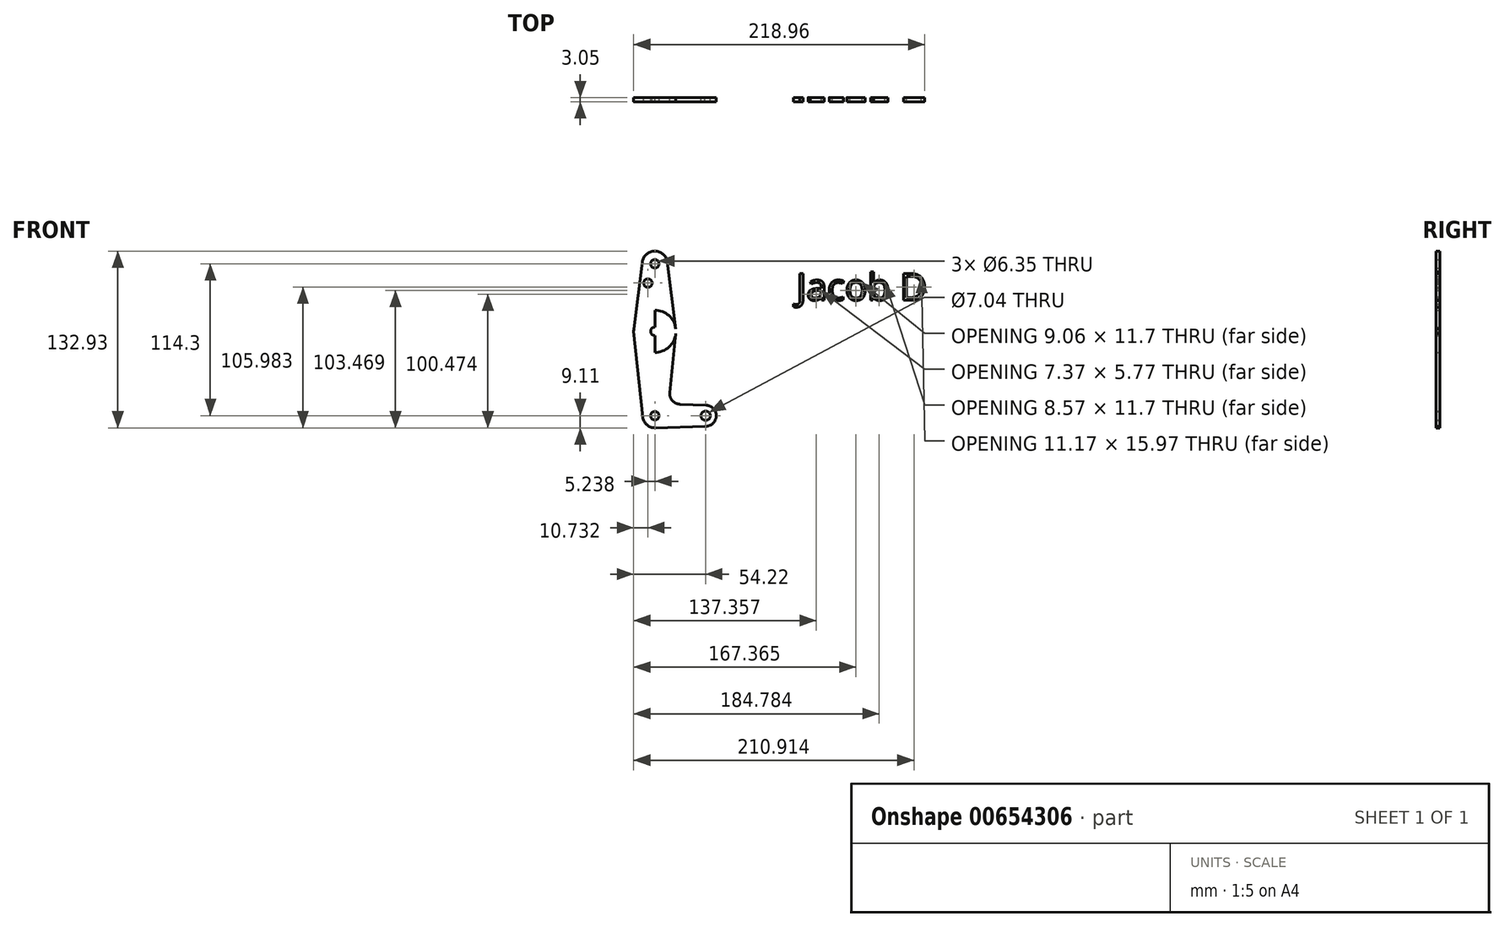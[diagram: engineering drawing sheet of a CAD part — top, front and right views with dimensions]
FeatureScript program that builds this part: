
annotation { "Feature Type Name" : "Feature", "Feature Type Description" : "" }
export const myFeature = defineFeature(function(context is Context, id is Id, definition is map)
    precondition{}
    {
        {
            var Q0;
            Q0=qCreatedBy(makeId("Front.planeOp"),FACE);
            var sketch = newSketch(context, id + "F0", { "sketchPlane" : qUnion([Q0])});
            skLineSegment(sketch, "E0", {"start": v(0, 50.8) * mm, "end": v(0, -63.5) * mm});
            skLineSegment(sketch, "E1", {"start": v(0, -63.5) * mm, "end": v(38.25, -63.5) * mm});
            skCircle(sketch, "E2", {"center": v(0, 50.8) * mm, "radius": 9.53 * mm});
            skCircle(sketch, "E3", {"center": v(0, 0) * mm, "radius": 15.88 * mm});
            skCircle(sketch, "E4", {"center": v(0, -63.5) * mm, "radius": 9.11 * mm});
            skCircle(sketch, "E5", {"center": v(38.25, -63.5) * mm, "radius": 7.94 * mm});
            skLineSegment(sketch, "E6", {"start": v(-15.78, 1.7) * mm, "end": v(-15.97, 0) * mm});
            skLineSegment(sketch, "E7", {"start": v(-15.97, 0) * mm, "end": v(-9.06, -64.47) * mm});
            skLineSegment(sketch, "E8", {"start": v(18.8, -54.84) * mm, "end": v(38.54, -55.57) * mm});
            skLineSegment(sketch, "E9", {"start": v(0.3, -72.6) * mm, "end": v(39.45, -71.35) * mm});
            skLineSegment(sketch, "E10", {"start": v(15.8, -1.63) * mm, "end": v(11.2, -46.08) * mm});
            skCircle(sketch, "E11", {"center": v(0, 50.8) * mm, "radius": 3.18 * mm});
            skCircle(sketch, "E12", {"center": v(-5.24, 36.31) * mm, "radius": 3.18 * mm});
            skCircle(sketch, "E13", {"center": v(38.25, -63.5) * mm, "radius": 3.52 * mm});
            skArc(sketch, "E14.filletArc", {"start": v(11.2, -46.08) * mm, "mid": v(13.1, -52.1) * mm, "end": v(18.8, -54.84) * mm});
            skCircle(sketch, "E15", {"center": v(0, -63.5) * mm, "radius": 3.18 * mm});
            skLineSegment(sketch, "E16", {"start": v(9.45, 52) * mm, "end": v(15.75, 1.98) * mm});
            skLineSegment(sketch, "E17", {"start": v(-9.45, 52) * mm, "end": v(-15.75, 1.98) * mm});
            skCircle(sketch, "E18", {"center": v(0, 0) * mm, "radius": 3.18 * mm});
            skText(sketch, "E19", { "text": "Jacob D", "fontName": "OpenSans-Regular.ttf"});
            const initialGuessF0  = {"E19": [0.10656, 0.02338, 1, 0, 0.02016]};
            skSetInitialGuess(sketch, initialGuessF0);
            skSolve(sketch);
        }
        {
            var Q0;
            {var subQ0=sQuery(id+"F0.wireOp",EDGE,"E7");Q0=makeQuery(id+"F0.imprint","IMPRINT",FACE,{"disambiguationData":[TD([[makeQuery(id+"F0.imprint","IMPRINT",EDGE,{"derivedFrom":subQ0}),1.0]])]});}
            var Q1;
            {var subQ0=sQuery(id+"F0.wireOp",EDGE,"E2");var subQ1=sQuery(id+"F0.wireOp",EDGE,"E0");var subQ2=makeQuery(id+"F0.imprint","INTERSECT",VERTEX,{"derivedFrom":[subQ1,subQ0]});Q1=makeQuery(id+"F0.imprint","IMPRINT",FACE,{"disambiguationData":[TD([[makeQuery(id+"F0.imprint","IMPRINT",EDGE,{"disambiguationData":[TD([[subQ2,-1.0]])],"derivedFrom":subQ1}),1.0]])]});}
            var Q2;
            Q2=makeQuery(id+"F0.imprint","IMPRINT",FACE,{"disambiguationData":[TD([[makeQuery(id+"F0.imprint","IMPRINT",EDGE,{"derivedFrom":sQuery(id+"F0.wireOp",EDGE,"E12")}),-1.0]])]});
            var Q3;
            Q3=makeQuery(id+"F0.imprint","IMPRINT",FACE,{"disambiguationData":[TD([[makeQuery(id+"F0.imprint","IMPRINT",EDGE,{"derivedFrom":sQuery(id+"F0.wireOp",EDGE,"E11")}),-1.0]])]});
            var Q4;
            {var subQ2=sQuery(id+"F0.wireOp",EDGE,"E3");var subQ6=sQuery(id+"F0.wireOp",EDGE,"E0");var subQ8=makeQuery(id+"F0.imprint","INTERSECT",VERTEX,{"disambiguationData":[OD(0.0)],"derivedFrom":[subQ6,subQ2]});Q4=makeQuery(id+"F0.imprint","IMPRINT",FACE,{"disambiguationData":[TD([[makeQuery(id+"F0.imprint","IMPRINT",EDGE,{"disambiguationData":[TD([[subQ8,-1.0]])],"derivedFrom":subQ6}),1.0]])]});}
            var Q5;
            {var subQ0=sQuery(id+"F0.wireOp",EDGE,"E3");var subQ1=sQuery(id+"F0.wireOp",EDGE,"E0");var subQ2=makeQuery(id+"F0.imprint","INTERSECT",VERTEX,{"disambiguationData":[OD(0.0)],"derivedFrom":[subQ1,subQ0]});Q5=makeQuery(id+"F0.imprint","IMPRINT",FACE,{"disambiguationData":[TD([[makeQuery(id+"F0.imprint","IMPRINT",EDGE,{"disambiguationData":[TD([[subQ2,-1.0]])],"derivedFrom":subQ1}),-1.0]])]});}
            var Q6;
            {var subQ0=sQuery(id+"F0.wireOp",EDGE,"E4");var subQ7=sQuery(id+"F0.wireOp",EDGE,"E0");var subQ8=makeQuery(id+"F0.imprint","INTERSECT",VERTEX,{"derivedFrom":[subQ7,subQ0]});Q6=makeQuery(id+"F0.imprint","IMPRINT",FACE,{"disambiguationData":[TD([[makeQuery(id+"F0.imprint","IMPRINT",EDGE,{"disambiguationData":[TD([[subQ8,-1.0]])],"derivedFrom":subQ7}),-1.0]])]});}
            var Q7;
            Q7=makeQuery(id+"F0.imprint","IMPRINT",FACE,{"disambiguationData":[TD([[makeQuery(id+"F0.imprint","IMPRINT",EDGE,{"derivedFrom":sQuery(id+"F0.wireOp",EDGE,"E13")}),-1.0]])]});
            var Q8;
            {var subQ0=sQuery(id+"F0.wireOp",EDGE,"E5");var subQ1=sQuery(id+"F0.wireOp",EDGE,"E1");var subQ2=makeQuery(id+"F0.imprint","INTERSECT",VERTEX,{"derivedFrom":[subQ1,subQ0]});Q8=makeQuery(id+"F0.imprint","IMPRINT",FACE,{"disambiguationData":[TD([[makeQuery(id+"F0.imprint","IMPRINT",EDGE,{"disambiguationData":[TD([[subQ2,1.0]])],"derivedFrom":subQ1}),-1.0]])]});}
            var Q9;
            {var subQ11=sQuery(id+"F0.wireOp",EDGE,"E8");Q9=makeQuery(id+"F0.imprint","IMPRINT",FACE,{"disambiguationData":[TD([[makeQuery(id+"F0.imprint","IMPRINT",EDGE,{"derivedFrom":subQ11}),-1.0]])]});}
            var Q10;
            {var subQ0=sQuery(id+"F0.wireOp",EDGE,"E4");var subQ1=sQuery(id+"F0.wireOp",EDGE,"E0");var subQ2=makeQuery(id+"F0.imprint","INTERSECT",VERTEX,{"derivedFrom":[subQ1,subQ0]});Q10=makeQuery(id+"F0.imprint","IMPRINT",FACE,{"disambiguationData":[TD([[makeQuery(id+"F0.imprint","IMPRINT",EDGE,{"disambiguationData":[TD([[subQ2,-1.0]])],"derivedFrom":subQ1}),1.0]])]});}
            var Q11;
            Q11=makeQuery(id+"F0.imprint","IMPRINT",FACE,{"disambiguationData":[TD([[makeQuery(id+"F0.imprint","IMPRINT",EDGE,{"derivedFrom":sQuery(id+"F0.wireOp",EDGE,"E19.sketch_text.stroke-0")}),-1.0]])]});
            var Q12;
            Q12=makeQuery(id+"F0.imprint","IMPRINT",FACE,{"disambiguationData":[TD([[makeQuery(id+"F0.imprint","IMPRINT",EDGE,{"derivedFrom":sQuery(id+"F0.wireOp",EDGE,"E19.sketch_text.stroke-10")}),-1.0]])]});
            var Q13;
            Q13=makeQuery(id+"F0.imprint","IMPRINT",FACE,{"disambiguationData":[TD([[makeQuery(id+"F0.imprint","IMPRINT",EDGE,{"derivedFrom":sQuery(id+"F0.wireOp",EDGE,"E19.sketch_text.stroke-37")}),-1.0]])]});
            var Q14;
            Q14=makeQuery(id+"F0.imprint","IMPRINT",FACE,{"disambiguationData":[TD([[makeQuery(id+"F0.imprint","IMPRINT",EDGE,{"derivedFrom":sQuery(id+"F0.wireOp",EDGE,"E19.sketch_text.stroke-52")}),-1.0]])]});
            var Q15;
            Q15=makeQuery(id+"F0.imprint","IMPRINT",FACE,{"disambiguationData":[TD([[makeQuery(id+"F0.imprint","IMPRINT",EDGE,{"derivedFrom":sQuery(id+"F0.wireOp",EDGE,"E19.sketch_text.stroke-69")}),-1.0]])]});
            var Q16;
            Q16=makeQuery(id+"F0.imprint","IMPRINT",FACE,{"disambiguationData":[TD([[makeQuery(id+"F0.imprint","IMPRINT",EDGE,{"derivedFrom":sQuery(id+"F0.wireOp",EDGE,"E19.sketch_text.stroke-92")}),-1.0]])]});
            extrude(context, id + "F1", {"entities" : qUnion([Q0, Q1, Q2, Q3, Q4, Q5, Q6, Q7, Q8, Q9, Q10, Q11, Q12, Q13, Q14, Q15, Q16]), "depth" : 3.05 * mm, "offsetDistance" : 25.4 * mm});
        }
        {
            var Q0;
            {var subQ5=sQuery(id+"F0.wireOp",EDGE,"E16");Q0=makeQuery(id+"F0.imprint","IMPRINT",FACE,{"disambiguationData":[TD([[makeQuery(id+"F0.imprint","IMPRINT",EDGE,{"derivedFrom":subQ5}),-1.0]])]});}
            var Q1;
            Q1=makeQuery(id+"F0.imprint","IMPRINT",FACE,{"disambiguationData":[TD([[makeQuery(id+"F0.imprint","IMPRINT",EDGE,{"derivedFrom":sQuery(id+"F0.wireOp",EDGE,"E12")}),-1.0]])]});
            var Q2;
            Q2=makeQuery(id+"F0.imprint","IMPRINT",FACE,{"disambiguationData":[TD([[makeQuery(id+"F0.imprint","IMPRINT",EDGE,{"derivedFrom":sQuery(id+"F0.wireOp",EDGE,"E12")}),-1.0]])]});
            var Q3;
            Q3=makeQuery(id+"F0.imprint","IMPRINT",FACE,{"disambiguationData":[TD([[makeQuery(id+"F0.imprint","IMPRINT",EDGE,{"derivedFrom":sQuery(id+"F0.wireOp",EDGE,"E13")}),-1.0]])]});
            var Q4;
            {var subQ0=sQuery(id+"F0.wireOp",EDGE,"E5");var subQ1=sQuery(id+"F0.wireOp",EDGE,"E1");var subQ2=makeQuery(id+"F0.imprint","INTERSECT",VERTEX,{"derivedFrom":[subQ1,subQ0]});Q4=makeQuery(id+"F0.imprint","IMPRINT",FACE,{"disambiguationData":[TD([[makeQuery(id+"F0.imprint","IMPRINT",EDGE,{"disambiguationData":[TD([[subQ2,1.0]])],"derivedFrom":subQ1}),-1.0]])]});}
            var Q5;
            {var subQ7=sQuery(id+"F0.wireOp",EDGE,"E8");Q5=makeQuery(id+"F0.imprint","IMPRINT",FACE,{"disambiguationData":[TD([[makeQuery(id+"F0.imprint","IMPRINT",EDGE,{"derivedFrom":subQ7}),-1.0]])]});}
            var Q6;
            {var subQ0=sQuery(id+"F0.wireOp",EDGE,"E3");var subQ3=sQuery(id+"F0.wireOp",EDGE,"E0");var subQ4=makeQuery(id+"F0.imprint","INTERSECT",VERTEX,{"disambiguationData":[OD(0.0)],"derivedFrom":[subQ3,subQ0]});Q6=makeQuery(id+"F0.imprint","IMPRINT",FACE,{"disambiguationData":[TD([[makeQuery(id+"F0.imprint","IMPRINT",EDGE,{"disambiguationData":[TD([[subQ4,-1.0]])],"derivedFrom":subQ3}),-1.0]])]});}
            var Q7;
            {var subQ0=sQuery(id+"F0.wireOp",EDGE,"E4");var subQ3=sQuery(id+"F0.wireOp",EDGE,"E0");var subQ4=makeQuery(id+"F0.imprint","INTERSECT",VERTEX,{"derivedFrom":[subQ3,subQ0]});Q7=makeQuery(id+"F0.imprint","IMPRINT",FACE,{"disambiguationData":[TD([[makeQuery(id+"F0.imprint","IMPRINT",EDGE,{"disambiguationData":[TD([[subQ4,-1.0]])],"derivedFrom":subQ3}),-1.0]])]});}
            var Q8;
            {var subQ0=sQuery(id+"F0.wireOp",EDGE,"E9");var subQ1=sQuery(id+"F0.wireOp",EDGE,"E5");var subQ2=makeQuery(id+"F0.imprint","INTERSECT",VERTEX,{"disambiguationData":[OD(0.0)],"derivedFrom":[subQ1,subQ0]});Q8=makeQuery(id+"F0.imprint","IMPRINT",FACE,{"disambiguationData":[TD([[makeQuery(id+"F0.imprint","IMPRINT",EDGE,{"disambiguationData":[TD([[subQ2,1.0]])],"derivedFrom":subQ1}),1.0]])]});}
            var Q9;
            {var subQ5=sQuery(id+"F0.wireOp",EDGE,"E16");Q9=makeQuery(id+"F0.imprint","IMPRINT",FACE,{"disambiguationData":[TD([[makeQuery(id+"F0.imprint","IMPRINT",EDGE,{"derivedFrom":subQ5}),-1.0]])]});}
            var Q10;
            {var subQ0=sQuery(id+"F0.wireOp",EDGE,"E6");Q10=makeQuery(id+"F0.imprint","IMPRINT",FACE,{"disambiguationData":[TD([[makeQuery(id+"F0.imprint","IMPRINT",EDGE,{"derivedFrom":subQ0}),1.0]])]});}
            var Q11;
            {var subQ0=sQuery(id+"F0.wireOp",EDGE,"E3");var subQ2=sQuery(id+"F0.wireOp",EDGE,"E0");var subQ5=makeQuery(id+"F0.imprint","INTERSECT",VERTEX,{"disambiguationData":[OD(0.0)],"derivedFrom":[subQ2,subQ0]});Q11=makeQuery(id+"F0.imprint","IMPRINT",FACE,{"disambiguationData":[TD([[makeQuery(id+"F0.imprint","IMPRINT",EDGE,{"disambiguationData":[TD([[subQ5,-1.0]])],"derivedFrom":subQ2}),1.0]])]});}
            var Q12;
            Q12=makeQuery(id+"F0.imprint","IMPRINT",FACE,{"disambiguationData":[TD([[makeQuery(id+"F0.imprint","IMPRINT",EDGE,{"derivedFrom":sQuery(id+"F0.wireOp",EDGE,"E11")}),-1.0]])]});
            var Q13;
            {var subQ0=sQuery(id+"F0.wireOp",EDGE,"E3");var subQ1=sQuery(id+"F0.wireOp",EDGE,"E0");var subQ2=makeQuery(id+"F0.imprint","INTERSECT",VERTEX,{"disambiguationData":[OD(1.0)],"derivedFrom":[subQ1,subQ0]});Q13=makeQuery(id+"F0.imprint","IMPRINT",FACE,{"disambiguationData":[TD([[makeQuery(id+"F0.imprint","IMPRINT",EDGE,{"disambiguationData":[TD([[subQ2,-1.0]])],"derivedFrom":subQ1}),-1.0]])]});}
            extrude(context, id + "F2", {"entities" : qUnion([Q0, Q1, Q2, Q3, Q4, Q5, Q6, Q7, Q8, Q9, Q10, Q11, Q12, Q13]), "operationType" : NewBodyOperationType.ADD, "depth" : 3.05 * mm, "offsetDistance" : 25.4 * mm});
        }
    });
